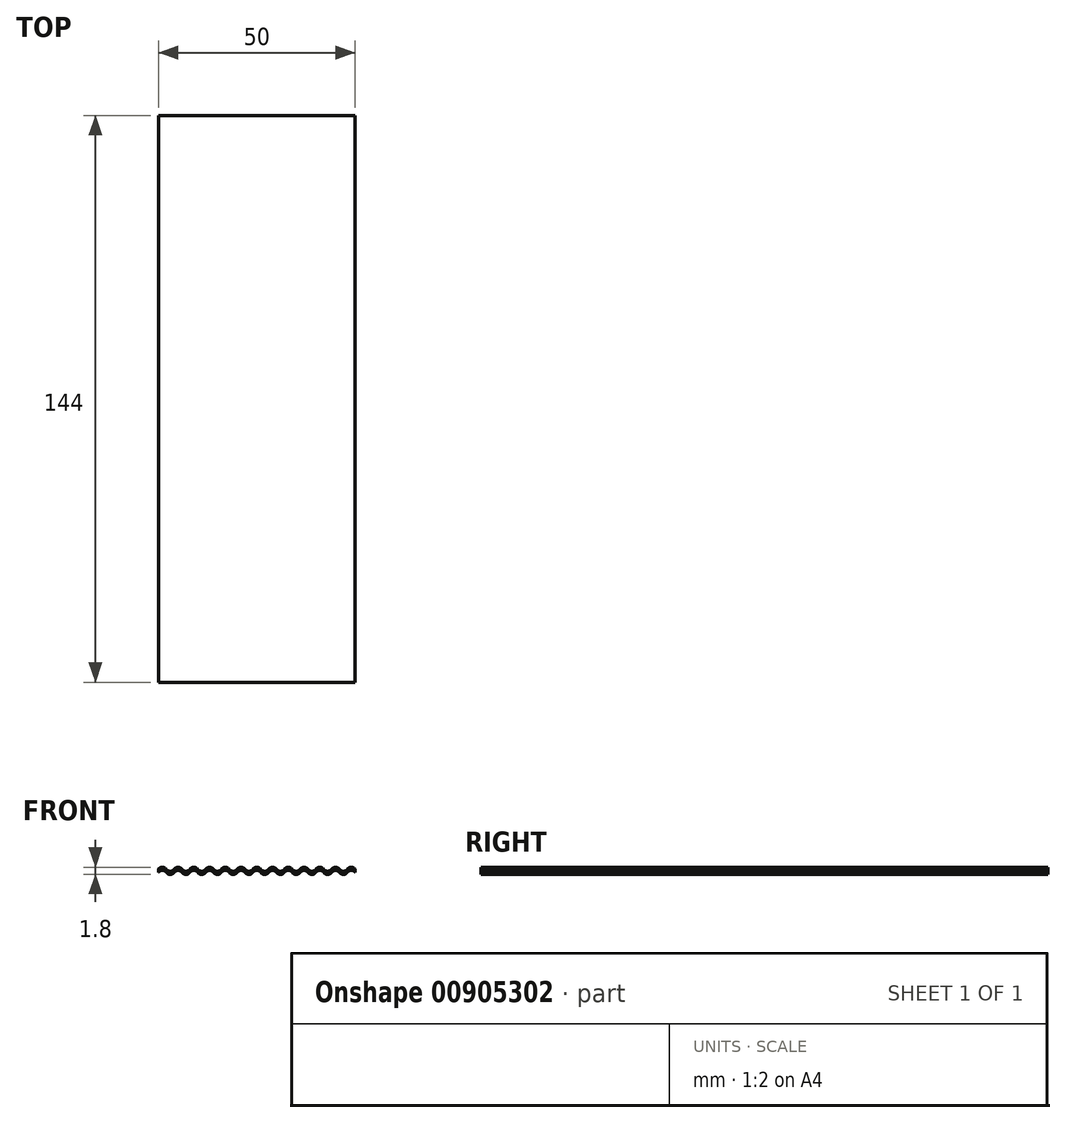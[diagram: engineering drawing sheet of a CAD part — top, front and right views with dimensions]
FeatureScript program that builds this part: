
annotation { "Feature Type Name" : "Feature", "Feature Type Description" : "" }
export const myFeature = defineFeature(function(context is Context, id is Id, definition is map)
    precondition{}
    {
        {
            var Q0;
            Q0=qCreatedBy(makeId("Front.planeOp"),FACE);
            var sketch = newSketch(context, id + "F0", { "sketchPlane" : qUnion([Q0])});
            skArc(sketch, "E0", {"start": v(-19, -0.4) * mm, "mid": v(-20, 0.1) * mm, "end": v(-21, -0.4) * mm});
            skArc(sketch, "E1", {"start": v(-23, -0.4) * mm, "mid": v(-22, -0.9) * mm, "end": v(-21, -0.4) * mm});
            skArc(sketch, "E2", {"start": v(-23, -0.4) * mm, "mid": v(-24, 0.1) * mm, "end": v(-25, -0.4) * mm});
            skArc(sketch, "E3", {"start": v(5, -0.4) * mm, "mid": v(6, -0.9) * mm, "end": v(7, -0.4) * mm});
            skArc(sketch, "E4", {"start": v(9, -0.4) * mm, "mid": v(8, 0.1) * mm, "end": v(7, -0.4) * mm});
            skArc(sketch, "E5", {"start": v(9, -0.4) * mm, "mid": v(10, -0.9) * mm, "end": v(11, -0.4) * mm});
            skArc(sketch, "E6", {"start": v(13, -0.4) * mm, "mid": v(12, 0.1) * mm, "end": v(11, -0.4) * mm});
            skArc(sketch, "E7", {"start": v(13, -0.4) * mm, "mid": v(14, -0.9) * mm, "end": v(15, -0.4) * mm});
            skArc(sketch, "E8", {"start": v(17, -0.4) * mm, "mid": v(16, 0.1) * mm, "end": v(15, -0.4) * mm});
            skArc(sketch, "E9", {"start": v(25, -0.4) * mm, "mid": v(24, 0.1) * mm, "end": v(23, -0.4) * mm});
            skArc(sketch, "E10", {"start": v(21, -0.4) * mm, "mid": v(22, -0.9) * mm, "end": v(23, -0.4) * mm});
            skArc(sketch, "E11", {"start": v(21, -0.4) * mm, "mid": v(20, 0.1) * mm, "end": v(19, -0.4) * mm});
            skArc(sketch, "E12", {"start": v(17, -0.4) * mm, "mid": v(18, -0.9) * mm, "end": v(19, -0.4) * mm});
            skArc(sketch, "E13", {"start": v(5, -0.4) * mm, "mid": v(4, 0.1) * mm, "end": v(3, -0.4) * mm});
            skArc(sketch, "E14", {"start": v(1, -0.4) * mm, "mid": v(2, -0.9) * mm, "end": v(3, -0.4) * mm});
            skArc(sketch, "E15", {"start": v(1, -0.4) * mm, "mid": v(0, 0.1) * mm, "end": v(-1, -0.4) * mm});
            skArc(sketch, "E16", {"start": v(-3, -0.4) * mm, "mid": v(-2, -0.9) * mm, "end": v(-1, -0.4) * mm});
            skArc(sketch, "E17", {"start": v(-3, -0.4) * mm, "mid": v(-4, 0.1) * mm, "end": v(-5, -0.4) * mm});
            skArc(sketch, "E18", {"start": v(-7, -0.4) * mm, "mid": v(-6, -0.9) * mm, "end": v(-5, -0.4) * mm});
            skArc(sketch, "E19", {"start": v(-7, -0.4) * mm, "mid": v(-8, 0.1) * mm, "end": v(-9, -0.4) * mm});
            skArc(sketch, "E20", {"start": v(-11, -0.4) * mm, "mid": v(-10, -0.9) * mm, "end": v(-9, -0.4) * mm});
            skArc(sketch, "E21", {"start": v(-11, -0.4) * mm, "mid": v(-12, 0.1) * mm, "end": v(-13, -0.4) * mm});
            skArc(sketch, "E22", {"start": v(-15, -0.4) * mm, "mid": v(-14, -0.9) * mm, "end": v(-13, -0.4) * mm});
            skArc(sketch, "E23", {"start": v(-15, -0.4) * mm, "mid": v(-16, 0.1) * mm, "end": v(-17, -0.4) * mm});
            skArc(sketch, "E24", {"start": v(-19, -0.4) * mm, "mid": v(-18, -0.9) * mm, "end": v(-17, -0.4) * mm});
            skArc(sketch, "E25", {"start": v(-19, 0.4) * mm, "mid": v(-20, 0.9) * mm, "end": v(-21, 0.4) * mm});
            skArc(sketch, "E26", {"start": v(-23, 0.4) * mm, "mid": v(-22, -0.1) * mm, "end": v(-21, 0.4) * mm});
            skArc(sketch, "E27", {"start": v(-23, 0.4) * mm, "mid": v(-24, 0.9) * mm, "end": v(-25, 0.4) * mm});
            skArc(sketch, "E28", {"start": v(5, 0.4) * mm, "mid": v(6, -0.1) * mm, "end": v(7, 0.4) * mm});
            skArc(sketch, "E29", {"start": v(9, 0.4) * mm, "mid": v(8, 0.9) * mm, "end": v(7, 0.4) * mm});
            skArc(sketch, "E30", {"start": v(9, 0.4) * mm, "mid": v(10, -0.1) * mm, "end": v(11, 0.4) * mm});
            skArc(sketch, "E31", {"start": v(13, 0.4) * mm, "mid": v(12, 0.9) * mm, "end": v(11, 0.4) * mm});
            skArc(sketch, "E32", {"start": v(13, 0.4) * mm, "mid": v(14, -0.1) * mm, "end": v(15, 0.4) * mm});
            skArc(sketch, "E33", {"start": v(17, 0.4) * mm, "mid": v(16, 0.9) * mm, "end": v(15, 0.4) * mm});
            skArc(sketch, "E34", {"start": v(25, 0.4) * mm, "mid": v(24, 0.9) * mm, "end": v(23, 0.4) * mm});
            skArc(sketch, "E35", {"start": v(21, 0.4) * mm, "mid": v(22, -0.1) * mm, "end": v(23, 0.4) * mm});
            skArc(sketch, "E36", {"start": v(21, 0.4) * mm, "mid": v(20, 0.9) * mm, "end": v(19, 0.4) * mm});
            skArc(sketch, "E37", {"start": v(17, 0.4) * mm, "mid": v(18, -0.1) * mm, "end": v(19, 0.4) * mm});
            skArc(sketch, "E38", {"start": v(5, 0.4) * mm, "mid": v(4, 0.9) * mm, "end": v(3, 0.4) * mm});
            skArc(sketch, "E39", {"start": v(1, 0.4) * mm, "mid": v(2, -0.1) * mm, "end": v(3, 0.4) * mm});
            skArc(sketch, "E40", {"start": v(1, 0.4) * mm, "mid": v(0, 0.9) * mm, "end": v(-1, 0.4) * mm});
            skArc(sketch, "E41", {"start": v(-3, 0.4) * mm, "mid": v(-2, -0.1) * mm, "end": v(-1, 0.4) * mm});
            skArc(sketch, "E42", {"start": v(-3, 0.4) * mm, "mid": v(-4, 0.9) * mm, "end": v(-5, 0.4) * mm});
            skArc(sketch, "E43", {"start": v(-7, 0.4) * mm, "mid": v(-6, -0.1) * mm, "end": v(-5, 0.4) * mm});
            skArc(sketch, "E44", {"start": v(-7, 0.4) * mm, "mid": v(-8, 0.9) * mm, "end": v(-9, 0.4) * mm});
            skArc(sketch, "E45", {"start": v(-11, 0.4) * mm, "mid": v(-10, -0.1) * mm, "end": v(-9, 0.4) * mm});
            skArc(sketch, "E46", {"start": v(-11, 0.4) * mm, "mid": v(-12, 0.9) * mm, "end": v(-13, 0.4) * mm});
            skArc(sketch, "E47", {"start": v(-15, 0.4) * mm, "mid": v(-14, -0.1) * mm, "end": v(-13, 0.4) * mm});
            skArc(sketch, "E48", {"start": v(-15, 0.4) * mm, "mid": v(-16, 0.9) * mm, "end": v(-17, 0.4) * mm});
            skArc(sketch, "E49", {"start": v(-19, 0.4) * mm, "mid": v(-18, -0.1) * mm, "end": v(-17, 0.4) * mm});
            skLineSegment(sketch, "E50", {"start": v(-25, 0.4) * mm, "end": v(-25, -0.4) * mm});
            skLineSegment(sketch, "E51", {"start": v(25, 0.4) * mm, "end": v(25, -0.4) * mm});
            skSolve(sketch);
        }
        {
            var Q0;
            Q0 = qSketchRegion(id + "F0", true);
            extrude(context, id + "F1", {"entities" : qUnion([Q0]), "depth" : 144 * mm, "offsetDistance" : 25 * mm});
        }
    });
